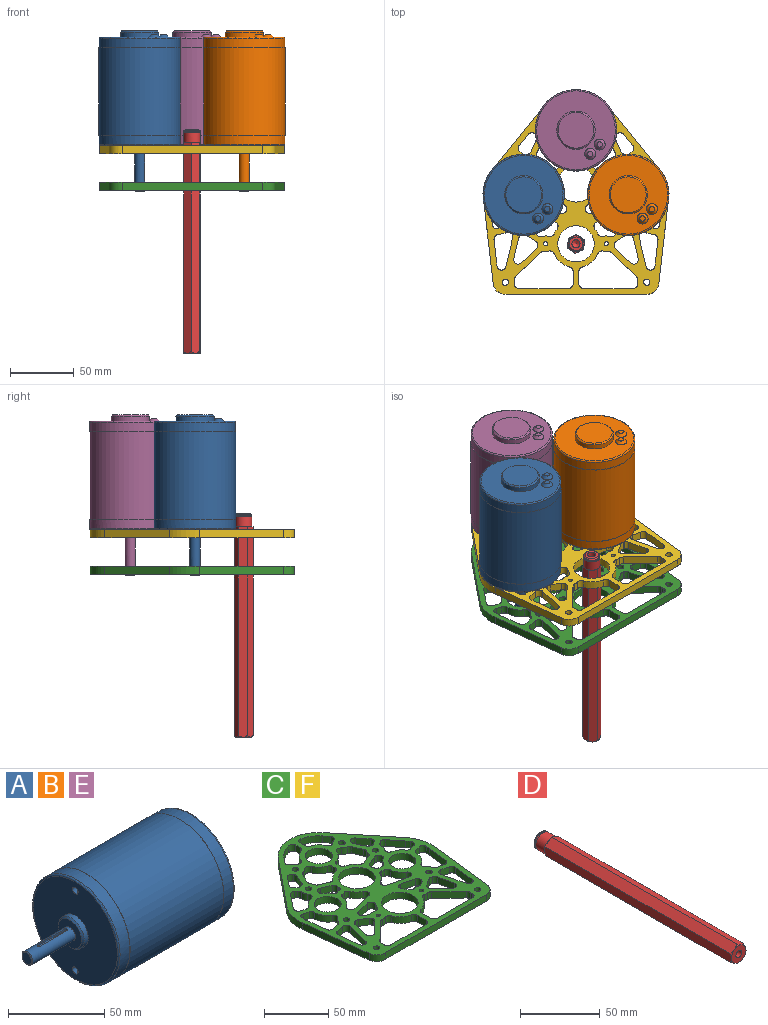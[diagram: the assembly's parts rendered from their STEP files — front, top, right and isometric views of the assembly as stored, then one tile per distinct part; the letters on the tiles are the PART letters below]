
ASSEMBLY  parts=6 mates=5
PART A: 33 faces, bbox 125.8x69x69 mm
  f0: cone r=4mm half-angle=45deg, axis (1,0,0), area 16.7mm2, adj f18,f22
  f1: cone r=9.53mm half-angle=45deg, axis (1,0,0), area 81.4mm2, adj f13,f27
  f2: cone r=14.02mm half-angle=45deg, axis (-1,0,0), area 131.2mm2, adj f17,f23
  f3: cone r=2.12mm half-angle=45deg, axis (-1,0,0), area 62.9mm2, adj f5,f29
  f4: cone r=2.12mm half-angle=45deg, axis (-1,0,0), area 62.9mm2, adj f6,f28
  f5: cylinder r=4.32mm len=8.64mm, axis (-1,0,0), area 1.3mm2, adj f3,f21
  f6: cylinder r=4.32mm len=8.64mm, axis (-1,0,0), area 1.3mm2, adj f4,f21
  f7: cone r=2.02mm half-angle=59deg, axis (-1,0,0), area 14.9mm2, adj f8
  f8: cylinder r=2.02mm len=13.61mm, axis (-1,0,0), area 172.7mm2, adj f7,f26
  f9: cone r=2.02mm half-angle=59deg, axis (-1,0,0), area 14.9mm2, adj f10
  f10: cylinder r=2.02mm len=13.61mm, axis (-1,0,0), area 172.7mm2, adj f9,f26
  f11: torus R=30.88mm, axis (1,0,0), area 311mm2, adj f16,f21
  f12: torus R=30.88mm, axis (-1,0,0), area 311mm2, adj f14,f26
  f13: cylinder r=9.53mm len=19.05mm, axis (1,0,0), area 178.6mm2, adj f1,f26
  f14: cylinder r=31.88mm len=63.75mm, axis (1,0,0), area 1448mm2, adj f12,f25
  f15: cylinder r=32mm len=68.76mm, axis (1,0,0), area 13826.1mm2, adj f24,f25
  f16: cylinder r=31.88mm len=63.75mm, axis (1,0,0), area 1448mm2, adj f11,f24
  f17: cylinder r=15.04mm len=30.07mm, axis (1,0,0), area 376.4mm2, adj f2,f21
  f18: cylinder r=4mm len=31.1mm, axis (1,0,0), area 739mm2, adj f0,f19,f20,f27,f31,f32
  f19: cylinder r=1mm len=2mm, axis (0,0,1), area 3.4mm2, adj f18,f30,f31,f32
  f20: cylinder r=1mm len=2mm, axis (0,0,-1), area 3.4mm2, adj f18,f30,f31,f32
  f21: plane 61.75x61.75mm, normal (1,0,0), area 2167.7mm2, adj f5,f6,f11,f17
  f22: plane 7x7mm, normal (-1,0,0), area 38.5mm2, adj f0
  f23: plane 28.04x28.04mm, normal (1,0,0), area 617.6mm2, adj f2
  f24: plane 64.01x64.01mm, normal (1,0,0), area 25.5mm2, adj f15,f16
  f25: plane 64.01x64.01mm, normal (-1,0,0), area 25.5mm2, adj f14,f15
  f26: plane 61.75x61.75mm, normal (-1,0,0), area 2684.5mm2, adj f8,f10,f12,f13
  f27: plane 17.02x17.02mm, normal (-1,0,0), area 177.2mm2, adj f1,f18
  f28: plane 4.24x4.24mm, normal (1,0,0), area 14.1mm2, adj f4
  f29: plane 4.24x4.24mm, normal (1,0,0), area 14.1mm2, adj f3
  f30: plane 21.5x2mm, normal (0,0,1), area 42.1mm2, adj f19,f20,f31,f32
  f31: plane 19.5x1.07mm, normal (0,-1,0), area 20.9mm2, adj f18,f19,f20,f30
  f32: plane 19.5x1.07mm, normal (0,1,0), area 20.9mm2, adj f18,f19,f20,f30
PART B: same geometry as A
PART C: 245 faces, bbox 145.6x160.4x6.4 mm
  f0: plane 160.41x145.59mm, normal (0,0,1), area 8119.2mm2, adj f2,f3,f4,f5,f6,f7,f8,f9
  f1: plane 160.41x145.59mm, normal (0,0,-1), area 8119.2mm2, adj f2,f3,f4,f5,f6,f7,f8,f9
  f2: plane 50.67x41.07mm, normal (-0.78,0.63,0), area 414.1mm2, adj f0,f1,f3,f26
  f3: cylinder r=31.75mm len=23.61mm, axis (0,0,-1), area 160.3mm2, adj f0,f1,f2,f4
  f4: plane 65.95x7.56mm, normal (-0.99,-0.11,0), area 421.5mm2, adj f0,f1,f3,f5
  f5: cylinder r=9.53mm len=10.07mm, axis (0,0,-1), area 92mm2, adj f0,f1,f4,f6
  f6: plane 110.52x6.35mm, normal (0,-1,0), area 701.8mm2, adj f0,f1,f5,f7
  f7: cylinder r=9.53mm len=9.46mm, axis (0,0,-1), area 88.1mm2, adj f0,f1,f6,f8
  f8: plane 65.95x7.56mm, normal (0.99,-0.11,0), area 421.5mm2, adj f0,f1,f7,f9
  f9: cylinder r=31.75mm len=23.61mm, axis (0,0,-1), area 160.3mm2, adj f0,f1,f8,f10
  f10: plane 50.67x41.07mm, normal (0.78,0.63,0), area 414.1mm2, adj f0,f1,f9,f26
  f11: cylinder r=14.27mm len=28.55mm, axis (0,0,-1), area 569.5mm2, adj f0,f1
  f12: cylinder r=14.27mm len=28.55mm, axis (0,0,-1), area 569.5mm2, adj f0,f1
  f13: cylinder r=10.52mm len=21.03mm, axis (0,0,-1), area 419.6mm2, adj f0,f1
  f14: cylinder r=10.52mm len=21.03mm, axis (0,0,-1), area 419.6mm2, adj f0,f1
  f15: cylinder r=2.49mm len=6.35mm, axis (0,0,-1), area 99.3mm2, adj f0,f1
  f16: cylinder r=2.49mm len=6.35mm, axis (0,0,-1), area 99.3mm2, adj f0,f1
  f17: cylinder r=1.59mm len=6.35mm, axis (0,0,-1), area 63.3mm2, adj f0,f1
  f18: cylinder r=1.59mm len=6.35mm, axis (0,0,-1), area 63.3mm2, adj f0,f1
  f19: cylinder r=2.49mm len=6.35mm, axis (0,0,-1), area 99.3mm2, adj f0,f1
  f20: cylinder r=2.49mm len=6.35mm, axis (0,0,-1), area 99.3mm2, adj f0,f1
  f21: cylinder r=2.49mm len=6.35mm, axis (0,0,-1), area 99.3mm2, adj f0,f1
  f22: cylinder r=2.49mm len=6.35mm, axis (0,0,-1), area 99.3mm2, adj f0,f1
  f23: cylinder r=2.49mm len=6.35mm, axis (0,0,-1), area 99.3mm2, adj f0,f1
  f24: cylinder r=2.49mm len=6.35mm, axis (0,0,-1), area 99.3mm2, adj f0,f1
  f25: cylinder r=10.52mm len=21.03mm, axis (0,0,-1), area 419.6mm2, adj f0,f1
  f26: cylinder r=31.72mm len=49.28mm, axis (0,0,-1), area 358.4mm2, adj f0,f1,f2,f10
  f27: plane 20.67x6.35mm, normal (0.99,0.11,0), area 132.1mm2, adj f0,f1,f30,f31
  f28: plane 22.48x6.35mm, normal (-0.97,0.23,0), area 146.7mm2, adj f0,f1,f30,f32
  f29: plane 7.68x6.35mm, normal (0.23,-0.97,0), area 50.1mm2, adj f0,f1,f31,f32
  f30: cylinder r=3.56mm len=6.99mm, axis (0,0,-1), area 63.1mm2, adj f0,f1,f27,f28
  f31: cylinder r=3.56mm len=6.35mm, axis (0,0,1), area 32.8mm2, adj f0,f1,f27,f29
  f32: cylinder r=3.56mm len=6.35mm, axis (0,0,1), area 45.9mm2, adj f0,f1,f28,f29
  f33: plane 6.35x5.15mm, normal (-1,0,0), area 32.7mm2, adj f0,f1,f38,f39
  f34: cylinder r=7.06mm len=6.35mm, axis (0,0,1), area 24.9mm2, adj f0,f1,f40,f41
  f35: plane 6.35x4.74mm, normal (0.78,-0.63,0), area 38.8mm2, adj f0,f1,f37,f41
  f36: cylinder r=15.09mm len=9.29mm, axis (0,0,1), area 83.7mm2, adj f0,f1,f38,f40
  f37: cylinder r=27.15mm len=14.37mm, axis (0,0,1), area 110.2mm2, adj f0,f1,f35,f39
  f38: cylinder r=3.56mm len=6.35mm, axis (0,0,1), area 28.3mm2, adj f0,f1,f33,f36
  f39: cylinder r=3.56mm len=6.35mm, axis (0,0,1), area 41.1mm2, adj f0,f1,f33,f37
  f40: cylinder r=3.56mm len=6.35mm, axis (0,0,1), area 46.4mm2, adj f0,f1,f34,f36
  f41: cylinder r=3.56mm len=6.35mm, axis (0,0,1), area 43.9mm2, adj f0,f1,f34,f35
  f42: cylinder r=15.09mm len=12.35mm, axis (0,0,1), area 94.7mm2, adj f0,f1,f48,f52
  f43: cylinder r=27.18mm len=6.35mm, axis (0,0,1), area 25.5mm2, adj f0,f1,f45,f49
  f44: cylinder r=7.06mm len=6.35mm, axis (0,0,1), area 30.6mm2, adj f0,f1,f50,f52
  f45: plane 20.33x6.35mm, normal (-0.99,0.11,0), area 129.9mm2, adj f0,f1,f43,f51
  f46: plane 6.9x6.35mm, normal (0.23,0.97,0), area 45mm2, adj f0,f1,f50,f51
  f47: plane 6.35x4.98mm, normal (0.28,-0.96,0), area 32.9mm2, adj f0,f1,f48,f49
  f48: cylinder r=3.56mm len=6.35mm, axis (0,0,1), area 28.3mm2, adj f0,f1,f42,f47
  f49: cylinder r=3.56mm len=6.35mm, axis (0,0,1), area 41.1mm2, adj f0,f1,f43,f47
  f50: cylinder r=3.56mm len=6.35mm, axis (0,0,1), area 22.3mm2, adj f0,f1,f44,f46
  f51: cylinder r=3.56mm len=6.35mm, axis (0,0,1), area 38.1mm2, adj f0,f1,f45,f46
  f52: cylinder r=3.56mm len=6.35mm, axis (0,0,1), area 46.4mm2, adj f0,f1,f42,f44
  f53: plane 6.35x4.98mm, normal (-0.28,-0.96,0), area 32.9mm2, adj f0,f1,f61,f62
  f54: cylinder r=27.18mm len=6.35mm, axis (0,0,1), area 25.5mm2, adj f0,f1,f55,f61
  f55: plane 20.33x6.35mm, normal (0.99,0.11,0), area 129.9mm2, adj f0,f1,f54,f60
  f56: cylinder r=15.09mm len=12.35mm, axis (0,0,1), area 94.7mm2, adj f0,f1,f62,f63
  f57: cylinder r=7.06mm len=6.35mm, axis (0,0,1), area 30.6mm2, adj f0,f1,f59,f63
  f58: plane 6.9x6.35mm, normal (-0.23,0.97,0), area 45mm2, adj f0,f1,f59,f60
  f59: cylinder r=3.56mm len=6.35mm, axis (0,0,1), area 22.3mm2, adj f0,f1,f57,f58
  f60: cylinder r=3.56mm len=6.35mm, axis (0,0,-1), area 38.1mm2, adj f0,f1,f55,f58
  f61: cylinder r=3.56mm len=6.35mm, axis (0,0,1), area 41.1mm2, adj f0,f1,f53,f54
  f62: cylinder r=3.56mm len=6.35mm, axis (0,0,1), area 28.3mm2, adj f0,f1,f53,f56
  f63: cylinder r=3.56mm len=6.35mm, axis (0,0,1), area 46.4mm2, adj f0,f1,f56,f57
  f64: plane 6.35x2.63mm, normal (1,0,0), area 16.7mm2, adj f0,f1,f75,f76
  f65: cylinder r=18.85mm len=9.72mm, axis (0,0,1), area 74.9mm2, adj f0,f1,f74,f75
  f66: cylinder r=7.06mm len=6.35mm, axis (0,0,1), area 18.2mm2, adj f0,f1,f72,f73
  f67: cylinder r=15.09mm len=9.29mm, axis (0,0,1), area 83.7mm2, adj f0,f1,f76,f77
  f68: cylinder r=7.06mm len=6.35mm, axis (0,0,1), area 31.4mm2, adj f0,f1,f71,f77
  f69: plane 8.91x6.35mm, normal (-0.41,0.91,0), area 61.9mm2, adj f0,f1,f73,f74
  f70: plane 9.44x6.35mm, normal (-0.91,-0.41,0), area 65.6mm2, adj f0,f1,f71,f72
  f71: cylinder r=3.56mm len=6.35mm, axis (0,0,1), area 22.3mm2, adj f0,f1,f68,f70
  f72: cylinder r=3.56mm len=6.35mm, axis (0,0,1), area 22.3mm2, adj f0,f1,f66,f70
  f73: cylinder r=3.56mm len=6.35mm, axis (0,0,1), area 22.3mm2, adj f0,f1,f66,f69
  f74: cylinder r=3.56mm len=6.35mm, axis (0,0,1), area 29.5mm2, adj f0,f1,f65,f69
  f75: cylinder r=3.56mm len=6.35mm, axis (0,0,1), area 29.5mm2, adj f0,f1,f64,f65
  f76: cylinder r=3.56mm len=6.35mm, axis (0,0,1), area 28.3mm2, adj f0,f1,f64,f67
  f77: cylinder r=3.56mm len=6.35mm, axis (0,0,1), area 46.4mm2, adj f0,f1,f67,f68
  f78: cylinder r=15.09mm len=9.29mm, axis (0,0,1), area 83.7mm2, adj f0,f1,f83,f86
  f79: cylinder r=27.15mm len=14.37mm, axis (0,0,1), area 110.2mm2, adj f0,f1,f81,f84
  f80: cylinder r=7.06mm len=6.35mm, axis (0,0,1), area 24.9mm2, adj f0,f1,f85,f86
  f81: plane 6.35x4.74mm, normal (-0.78,-0.63,0), area 38.8mm2, adj f0,f1,f79,f85
  f82: plane 6.35x5.15mm, normal (1,0,0), area 32.7mm2, adj f0,f1,f83,f84
  f83: cylinder r=3.56mm len=6.35mm, axis (0,0,1), area 28.3mm2, adj f0,f1,f78,f82
  f84: cylinder r=3.56mm len=6.35mm, axis (0,0,1), area 41.1mm2, adj f0,f1,f79,f82
  f85: cylinder r=3.56mm len=6.35mm, axis (0,0,1), area 43.9mm2, adj f0,f1,f80,f81
  f86: cylinder r=3.56mm len=6.35mm, axis (0,0,1), area 46.4mm2, adj f0,f1,f78,f80
  f87: cylinder r=18.85mm len=6.35mm, axis (0,0,1), area 29.3mm2, adj f0,f1,f92,f93
  f88: cylinder r=6.16mm len=6.35mm, axis (0,0,1), area 28.3mm2, adj f0,f1,f91,f93
  f89: plane 6.35x2.89mm, normal (-0.53,0.85,0), area 21.5mm2, adj f0,f1,f91,f94
  f90: plane 12.59x6.35mm, normal (-0.23,-0.97,0), area 82.1mm2, adj f0,f1,f92,f94
  f91: cylinder r=3.56mm len=6.35mm, axis (0,0,1), area 20.9mm2, adj f0,f1,f88,f89
  f92: cylinder r=3.56mm len=6.35mm, axis (0,0,1), area 55.7mm2, adj f0,f1,f87,f90
  f93: cylinder r=3.56mm len=6.35mm, axis (0,0,1), area 34mm2, adj f0,f1,f87,f88
  f94: cylinder r=3.56mm len=6.49mm, axis (0,0,1), area 53.2mm2, adj f0,f1,f89,f90
  f95: cylinder r=18.85mm len=7.91mm, axis (0,0,1), area 71mm2, adj f0,f1,f101,f102
  f96: cylinder r=15.09mm len=11.01mm, axis (0,0,1), area 84.8mm2, adj f0,f1,f99,f100
  f97: plane 6.35x2.57mm, normal (0.21,-0.98,0), area 16.7mm2, adj f0,f1,f100,f102
  f98: plane 20.07x6.35mm, normal (-0.23,0.97,0), area 130.9mm2, adj f0,f1,f99,f101
  f99: cylinder r=3.56mm len=6.54mm, axis (0,0,1), area 63.2mm2, adj f0,f1,f96,f98
  f100: cylinder r=3.56mm len=6.35mm, axis (0,0,1), area 28.3mm2, adj f0,f1,f96,f97
  f101: cylinder r=3.56mm len=6.58mm, axis (0,0,1), area 54.3mm2, adj f0,f1,f95,f98
  f102: cylinder r=3.56mm len=6.35mm, axis (0,0,1), area 29.5mm2, adj f0,f1,f95,f97
  f103: cylinder r=15.09mm len=11.01mm, axis (0,0,1), area 84.8mm2, adj f0,f1,f109,f110
  f104: cylinder r=18.85mm len=7.91mm, axis (0,0,1), area 71mm2, adj f0,f1,f107,f108
  f105: plane 20.07x6.35mm, normal (0.23,0.97,0), area 130.9mm2, adj f0,f1,f108,f110
  f106: plane 6.35x2.57mm, normal (-0.21,-0.98,0), area 16.7mm2, adj f0,f1,f107,f109
  f107: cylinder r=3.56mm len=6.35mm, axis (0,0,1), area 29.5mm2, adj f0,f1,f104,f106
  f108: cylinder r=3.56mm len=6.58mm, axis (0,0,1), area 54.3mm2, adj f0,f1,f104,f105
  f109: cylinder r=3.56mm len=6.35mm, axis (0,0,1), area 28.3mm2, adj f0,f1,f103,f106
  f110: cylinder r=3.56mm len=6.54mm, axis (0,0,1), area 63.2mm2, adj f0,f1,f103,f105
  f111: cylinder r=18.85mm len=6.35mm, axis (0,0,1), area 11.9mm2, adj f0,f1,f118,f119
  f112: cylinder r=15.09mm len=6.35mm, axis (0,0,1), area 47.5mm2, adj f0,f1,f116,f120
  f113: cylinder r=7.06mm len=6.35mm, axis (0,0,1), area 1.5mm2, adj f0,f1,f117,f120
  f114: plane 8.91x6.35mm, normal (-0.41,-0.91,0), area 61.9mm2, adj f0,f1,f117,f119
  f115: plane 6.35x2.57mm, normal (-0.21,0.98,0), area 16.7mm2, adj f0,f1,f116,f118
  f116: cylinder r=3.56mm len=6.35mm, axis (0,0,1), area 28.3mm2, adj f0,f1,f112,f115
  f117: cylinder r=3.56mm len=6.35mm, axis (0,0,1), area 22.3mm2, adj f0,f1,f113,f114
  f118: cylinder r=3.56mm len=6.35mm, axis (0,0,1), area 29.5mm2, adj f0,f1,f111,f115
  f119: cylinder r=3.56mm len=6.35mm, axis (0,0,1), area 29.5mm2, adj f0,f1,f111,f114
  f120: cylinder r=3.56mm len=6.35mm, axis (0,0,1), area 46.4mm2, adj f0,f1,f112,f113
  f121: plane 7.35x6.35mm, normal (-0.53,-0.85,0), area 54.8mm2, adj f0,f1,f127,f129
  f122: cylinder r=6.16mm len=6.35mm, axis (0,0,1), area 0.9mm2, adj f0,f1,f128,f129
  f123: cylinder r=7.06mm len=6.35mm, axis (0,0,1), area 3.8mm2, adj f0,f1,f126,f127
  f124: plane 15.73x6.35mm, normal (0.97,-0.23,0), area 102.6mm2, adj f0,f1,f126,f130
  f125: plane 11.91x11.31mm, normal (-0.69,0.72,0), area 104.3mm2, adj f0,f1,f128,f130
  f126: cylinder r=3.56mm len=6.35mm, axis (0,0,1), area 22.3mm2, adj f0,f1,f123,f124
  f127: cylinder r=3.56mm len=6.35mm, axis (0,0,1), area 22.3mm2, adj f0,f1,f121,f123
  f128: cylinder r=3.56mm len=6.35mm, axis (0,0,1), area 20.9mm2, adj f0,f1,f122,f125
  f129: cylinder r=3.56mm len=6.35mm, axis (0,0,1), area 20.9mm2, adj f0,f1,f121,f122
  f130: cylinder r=3.56mm len=6.35mm, axis (0,0,1), area 57.9mm2, adj f0,f1,f124,f125
  f131: cylinder r=18.85mm len=6.35mm, axis (0,0,1), area 29.3mm2, adj f0,f1,f136,f137
  f132: cylinder r=6.16mm len=6.35mm, axis (0,0,1), area 28.3mm2, adj f0,f1,f135,f137
  f133: plane 12.59x6.35mm, normal (0.23,-0.97,0), area 82.1mm2, adj f0,f1,f136,f138
  f134: plane 6.35x2.89mm, normal (0.53,0.85,0), area 21.5mm2, adj f0,f1,f135,f138
  f135: cylinder r=3.56mm len=6.35mm, axis (0,0,1), area 20.9mm2, adj f0,f1,f132,f134
  f136: cylinder r=3.56mm len=6.35mm, axis (0,0,1), area 55.7mm2, adj f0,f1,f131,f133
  f137: cylinder r=3.56mm len=6.35mm, axis (0,0,-1), area 34mm2, adj f0,f1,f131,f132
  f138: cylinder r=3.56mm len=6.49mm, axis (0,0,1), area 53.2mm2, adj f0,f1,f133,f134
  f139: plane 7.35x6.35mm, normal (0.53,-0.85,0), area 54.8mm2, adj f0,f1,f145,f147
  f140: cylinder r=6.16mm len=6.35mm, axis (0,0,1), area 0.9mm2, adj f0,f1,f146,f147
  f141: cylinder r=7.06mm len=6.35mm, axis (0,0,1), area 3.8mm2, adj f0,f1,f144,f145
  f142: plane 11.91x11.31mm, normal (0.69,0.72,0), area 104.3mm2, adj f0,f1,f146,f148
  f143: plane 15.73x6.35mm, normal (-0.97,-0.23,0), area 102.6mm2, adj f0,f1,f144,f148
  f144: cylinder r=3.56mm len=6.35mm, axis (0,0,1), area 22.3mm2, adj f0,f1,f141,f143
  f145: cylinder r=3.56mm len=6.35mm, axis (0,0,1), area 22.3mm2, adj f0,f1,f139,f141
  f146: cylinder r=3.56mm len=6.35mm, axis (0,0,1), area 20.9mm2, adj f0,f1,f140,f142
  f147: cylinder r=3.56mm len=6.35mm, axis (0,0,1), area 20.9mm2, adj f0,f1,f139,f140
  f148: cylinder r=3.56mm len=6.35mm, axis (0,0,1), area 57.9mm2, adj f0,f1,f142,f143
  f149: plane 7.68x6.35mm, normal (-0.23,-0.97,0), area 50.1mm2, adj f0,f1,f152,f154
  f150: plane 22.48x6.35mm, normal (0.97,0.23,0), area 146.7mm2, adj f0,f1,f153,f154
  f151: plane 20.67x6.35mm, normal (-0.99,0.11,0), area 132.1mm2, adj f0,f1,f152,f153
  f152: cylinder r=3.56mm len=6.35mm, axis (0,0,-1), area 32.8mm2, adj f0,f1,f149,f151
  f153: cylinder r=3.56mm len=6.99mm, axis (0,0,1), area 63.1mm2, adj f0,f1,f150,f151
  f154: cylinder r=3.56mm len=6.35mm, axis (0,0,1), area 45.9mm2, adj f0,f1,f149,f150
  f155: plane 9.44x6.35mm, normal (0.91,-0.41,0), area 65.6mm2, adj f0,f1,f166,f167
  f156: cylinder r=7.06mm len=6.35mm, axis (0,0,1), area 18.2mm2, adj f0,f1,f162,f166
  f157: cylinder r=18.85mm len=9.72mm, axis (0,0,1), area 74.9mm2, adj f0,f1,f163,f164
  f158: cylinder r=7.06mm len=6.35mm, axis (0,0,1), area 31.4mm2, adj f0,f1,f167,f168
  f159: cylinder r=15.09mm len=9.29mm, axis (0,0,1), area 83.7mm2, adj f0,f1,f165,f168
  f160: plane 6.35x2.63mm, normal (-1,0,0), area 16.7mm2, adj f0,f1,f164,f165
  f161: plane 8.91x6.35mm, normal (0.41,0.91,0), area 61.9mm2, adj f0,f1,f162,f163
  f162: cylinder r=3.56mm len=6.35mm, axis (0,0,1), area 22.3mm2, adj f0,f1,f156,f161
  f163: cylinder r=3.56mm len=6.35mm, axis (0,0,1), area 29.5mm2, adj f0,f1,f157,f161
  f164: cylinder r=3.56mm len=6.35mm, axis (0,0,1), area 29.5mm2, adj f0,f1,f157,f160
  f165: cylinder r=3.56mm len=6.35mm, axis (0,0,1), area 28.3mm2, adj f0,f1,f159,f160
  f166: cylinder r=3.56mm len=6.35mm, axis (0,0,1), area 22.3mm2, adj f0,f1,f155,f156
  f167: cylinder r=3.56mm len=6.35mm, axis (0,0,1), area 22.3mm2, adj f0,f1,f155,f158
  f168: cylinder r=3.56mm len=6.35mm, axis (0,0,1), area 46.4mm2, adj f0,f1,f158,f159
  f169: plane 12.66x10.26mm, normal (0.78,-0.63,0), area 103.5mm2, adj f0,f1,f170,f176
  f170: cylinder r=27.18mm len=6.35mm, axis (0,0,1), area 25.5mm2, adj f0,f1,f169,f177
  f171: cylinder r=15.09mm len=9.29mm, axis (0,0,1), area 72.7mm2, adj f0,f1,f178,f179
  f172: cylinder r=7.06mm len=6.35mm, axis (0,0,1), area 35.6mm2, adj f0,f1,f175,f179
  f173: plane 6.35x4.98mm, normal (0.28,0.96,0), area 32.9mm2, adj f0,f1,f177,f178
  f174: plane 6.35x1.79mm, normal (-0.63,-0.78,0), area 14.6mm2, adj f0,f1,f175,f176
  f175: cylinder r=3.56mm len=6.35mm, axis (0,0,1), area 22.3mm2, adj f0,f1,f172,f174
  f176: cylinder r=3.56mm len=6.35mm, axis (0,0,1), area 35.5mm2, adj f0,f1,f169,f174
  f177: cylinder r=3.56mm len=6.35mm, axis (0,0,1), area 41.1mm2, adj f0,f1,f170,f173
  f178: cylinder r=3.56mm len=6.35mm, axis (0,0,1), area 28.3mm2, adj f0,f1,f171,f173
  f179: cylinder r=3.56mm len=6.35mm, axis (0,0,1), area 46.4mm2, adj f0,f1,f171,f172
  f180: plane 6.35x4.98mm, normal (-0.28,0.96,0), area 32.9mm2, adj f0,f1,f188,f189
  f181: cylinder r=27.18mm len=6.35mm, axis (0,0,1), area 25.5mm2, adj f0,f1,f182,f189
  f182: plane 12.66x10.26mm, normal (-0.78,-0.63,0), area 103.5mm2, adj f0,f1,f181,f187
  f183: cylinder r=7.06mm len=6.35mm, axis (0,0,1), area 35.6mm2, adj f0,f1,f186,f190
  f184: cylinder r=15.09mm len=9.29mm, axis (0,0,1), area 72.7mm2, adj f0,f1,f188,f190
  f185: plane 6.35x1.79mm, normal (0.63,-0.78,0), area 14.6mm2, adj f0,f1,f186,f187
  f186: cylinder r=3.56mm len=6.35mm, axis (0,0,1), area 22.3mm2, adj f0,f1,f183,f185
  f187: cylinder r=3.56mm len=6.35mm, axis (0,0,-1), area 35.5mm2, adj f0,f1,f182,f185
  f188: cylinder r=3.56mm len=6.35mm, axis (0,0,1), area 28.3mm2, adj f0,f1,f180,f184
  f189: cylinder r=3.56mm len=6.35mm, axis (0,0,1), area 41.1mm2, adj f0,f1,f180,f181
  f190: cylinder r=3.56mm len=6.35mm, axis (0,0,1), area 46.4mm2, adj f0,f1,f183,f184
  f191: plane 9.92x6.35mm, normal (1,0,0), area 63mm2, adj f0,f1,f199,f200
  f192: plane 39.2x6.35mm, normal (0,1,0), area 248.9mm2, adj f0,f1,f199,f202
  f193: cylinder r=7.06mm len=6.35mm, axis (0,0,1), area 13.9mm2, adj f0,f1,f198,f202
  f194: cylinder r=18.85mm len=12.3mm, axis (0,0,1), area 106.2mm2, adj f0,f1,f200,f201
  f195: cylinder r=6.16mm len=6.35mm, axis (0,0,1), area 20.3mm2, adj f0,f1,f197,f201
  f196: plane 19.69x18.71mm, normal (-0.69,-0.72,0), area 172.5mm2, adj f0,f1,f197,f198
  f197: cylinder r=3.56mm len=6.35mm, axis (0,0,1), area 20.9mm2, adj f0,f1,f195,f196
  f198: cylinder r=3.56mm len=6.35mm, axis (0,0,1), area 22.3mm2, adj f0,f1,f193,f196
  f199: cylinder r=3.56mm len=6.35mm, axis (0,0,1), area 35.5mm2, adj f0,f1,f191,f192
  f200: cylinder r=3.56mm len=6.35mm, axis (0,0,1), area 29.5mm2, adj f0,f1,f191,f194
  f201: cylinder r=3.56mm len=6.35mm, axis (0,0,1), area 34mm2, adj f0,f1,f194,f195
  f202: cylinder r=3.56mm len=6.35mm, axis (0,0,1), area 38.4mm2, adj f0,f1,f192,f193
  f203: plane 6.35x2.57mm, normal (0.21,0.98,0), area 16.7mm2, adj f0,f1,f210,f211
  f204: cylinder r=18.85mm len=6.35mm, axis (0,0,1), area 11.9mm2, adj f0,f1,f209,f210
  f205: cylinder r=15.09mm len=6.35mm, axis (0,0,1), area 47.5mm2, adj f0,f1,f211,f212
  f206: cylinder r=7.06mm len=6.35mm, axis (0,0,1), area 1.5mm2, adj f0,f1,f208,f212
  f207: plane 8.91x6.35mm, normal (0.41,-0.91,0), area 61.9mm2, adj f0,f1,f208,f209
  f208: cylinder r=3.56mm len=6.35mm, axis (0,0,1), area 22.3mm2, adj f0,f1,f206,f207
  f209: cylinder r=3.56mm len=6.35mm, axis (0,0,1), area 29.5mm2, adj f0,f1,f204,f207
  f210: cylinder r=3.56mm len=6.35mm, axis (0,0,1), area 29.5mm2, adj f0,f1,f203,f204
  f211: cylinder r=3.56mm len=6.35mm, axis (0,0,1), area 28.3mm2, adj f0,f1,f203,f205
  f212: cylinder r=3.56mm len=6.35mm, axis (0,0,1), area 46.4mm2, adj f0,f1,f205,f206
  f213: cylinder r=7.06mm len=6.35mm, axis (0,0,1), area 6.4mm2, adj f0,f1,f218,f220
  f214: cylinder r=7.06mm len=6.35mm, axis (0,0,1), area 2.4mm2, adj f0,f1,f221,f222
  f215: plane 8.82x7.15mm, normal (0.78,-0.63,0), area 72.1mm2, adj f0,f1,f219,f222
  f216: plane 9.44x6.35mm, normal (-0.91,0.41,0), area 65.6mm2, adj f0,f1,f220,f221
  f217: plane 6.35x1.79mm, normal (0.63,0.78,0), area 14.6mm2, adj f0,f1,f218,f219
  f218: cylinder r=3.56mm len=6.35mm, axis (0,0,1), area 22.3mm2, adj f0,f1,f213,f217
  f219: cylinder r=3.56mm len=6.35mm, axis (0,0,-1), area 35.5mm2, adj f0,f1,f215,f217
  f220: cylinder r=3.56mm len=6.35mm, axis (0,0,1), area 22.3mm2, adj f0,f1,f213,f216
  f221: cylinder r=3.56mm len=6.35mm, axis (0,0,1), area 22.3mm2, adj f0,f1,f214,f216
  f222: cylinder r=3.56mm len=6.35mm, axis (0,0,1), area 43.9mm2, adj f0,f1,f214,f215
  f223: plane 6.35x1.79mm, normal (-0.63,0.78,0), area 14.6mm2, adj f0,f1,f230,f231
  f224: plane 8.82x7.15mm, normal (-0.78,-0.63,0), area 72.1mm2, adj f0,f1,f231,f232
  f225: cylinder r=7.06mm len=6.35mm, axis (0,0,1), area 2.4mm2, adj f0,f1,f228,f232
  f226: cylinder r=7.06mm len=6.35mm, axis (0,0,1), area 6.4mm2, adj f0,f1,f229,f230
  f227: plane 9.44x6.35mm, normal (0.91,0.41,0), area 65.6mm2, adj f0,f1,f228,f229
  f228: cylinder r=3.56mm len=6.35mm, axis (0,0,1), area 22.3mm2, adj f0,f1,f225,f227
  f229: cylinder r=3.56mm len=6.35mm, axis (0,0,1), area 22.3mm2, adj f0,f1,f226,f227
  f230: cylinder r=3.56mm len=6.35mm, axis (0,0,1), area 22.3mm2, adj f0,f1,f223,f226
  f231: cylinder r=3.56mm len=6.35mm, axis (0,0,1), area 35.5mm2, adj f0,f1,f223,f224
  f232: cylinder r=3.56mm len=6.35mm, axis (0,0,1), area 43.9mm2, adj f0,f1,f224,f225
  f233: plane 39.19x6.35mm, normal (0,1,0), area 248.9mm2, adj f0,f1,f241,f243
  f234: cylinder r=7.06mm len=6.35mm, axis (0,0,1), area 13.8mm2, adj f0,f1,f239,f243
  f235: cylinder r=18.85mm len=12.3mm, axis (0,0,1), area 106.2mm2, adj f0,f1,f242,f244
  f236: cylinder r=6.16mm len=6.35mm, axis (0,0,1), area 20.3mm2, adj f0,f1,f240,f244
  f237: plane 9.92x6.35mm, normal (-1,0,0), area 63mm2, adj f0,f1,f241,f242
  f238: plane 19.69x18.71mm, normal (0.69,-0.72,0), area 172.5mm2, adj f0,f1,f239,f240
  f239: cylinder r=3.56mm len=6.35mm, axis (0,0,1), area 22.3mm2, adj f0,f1,f234,f238
  f240: cylinder r=3.56mm len=6.35mm, axis (0,0,1), area 20.9mm2, adj f0,f1,f236,f238
  f241: cylinder r=3.56mm len=6.35mm, axis (0,0,-1), area 35.5mm2, adj f0,f1,f233,f237
  f242: cylinder r=3.56mm len=6.35mm, axis (0,0,1), area 29.5mm2, adj f0,f1,f235,f237
  f243: cylinder r=3.56mm len=6.35mm, axis (0,0,1), area 38.4mm2, adj f0,f1,f233,f234
  f244: cylinder r=3.56mm len=6.35mm, axis (0,0,-1), area 34mm2, adj f0,f1,f235,f236
PART D: 25 faces, bbox 15.1x176.1x15.2 mm
  f0: cylinder r=2.55mm len=50.8mm, axis (0,-1,0), area 814.8mm2, adj f1,f17
  f1: cone r=2.55mm half-angle=59deg, axis (0,-1,0), area 23.9mm2, adj f0
  f2: cone r=5.34mm half-angle=45deg, axis (0,-1,0), area 51.9mm2, adj f6,f19
  f3: cone r=6.42mm half-angle=30deg, axis (0,1,0), area 4.7mm2, adj f12,f13,f17
  f4: cylinder r=3.19mm len=12.7mm, axis (0,1,0), area 254.4mm2, adj f5,f19
  f5: cone r=3.19mm half-angle=59deg, axis (0,1,0), area 37.2mm2, adj f4
  f6: cylinder r=6.34mm len=12.67mm, axis (0,-1,0), area 23.4mm2, adj f2,f18
  f7: cylinder r=5.94mm len=11.89mm, axis (0,-1,0), area 37.9mm2, adj f9,f18
  f8: cylinder r=6.34mm len=12.67mm, axis (0,-1,0), area 316.1mm2, adj f9,f10
  f9: plane 12.67x12.67mm, normal (0,1,0), area 15.2mm2, adj f7,f8
  f10: plane 14.61x13.28mm, normal (0,1,0), area 13.5mm2, adj f8,f11,f12,f13,f14,f15,f16
  f11: plane 165.61x7.81mm, normal (1,0,0.09), area 1207mm2, adj f10,f12,f16,f17,f21,f22
  f12: plane 165.61x7.15mm, normal (0.42,0,0.91), area 1207mm2, adj f3,f10,f11,f13,f17,f22
  f13: plane 165.61x6.52mm, normal (-0.57,0,0.82), area 1207mm2, adj f3,f10,f12,f14,f17,f23
  f14: plane 165.61x7.81mm, normal (-1,0,-0.09), area 1207mm2, adj f10,f13,f15,f17,f23,f24
  f15: plane 165.61x7.15mm, normal (-0.42,0,-0.91), area 1207.3mm2, adj f10,f14,f16,f17,f20,f24
  f16: plane 165.61x6.52mm, normal (0.57,0,-0.82), area 1207mm2, adj f10,f11,f15,f17,f20,f21
  f17: plane 12.83x12.81mm, normal (0,-1,0), area 108.4mm2, adj f0,f3,f11,f12,f13,f14,f15,f16
  f18: plane 12.67x12.67mm, normal (0,-1,0), area 15.2mm2, adj f6,f7
  f19: plane 10.67x10.67mm, normal (0,1,0), area 57.6mm2, adj f2,f4
  f20: cone r=6.42mm half-angle=30deg, axis (0,1,0), area 4.7mm2, adj f15,f16,f17
  f21: cone r=6.42mm half-angle=30deg, axis (0,1,0), area 4.7mm2, adj f11,f16,f17
  f22: cone r=6.42mm half-angle=30deg, axis (0,1,0), area 4.7mm2, adj f11,f12,f17
  f23: cone r=6.42mm half-angle=30deg, axis (0,1,0), area 4.7mm2, adj f13,f14,f17
  f24: cone r=6.42mm half-angle=30deg, axis (0,1,0), area 4.7mm2, adj f14,f15,f17
PART E: same geometry as A
PART F: same geometry as C
PLACE A rot(axis=(0.71,0,0.71),180deg) t=(-67.99,12.65,48.8)mm
PLACE B rot(axis=(0.71,0,0.71),180deg) t=(14.09,12.65,48.8)mm
PLACE C t=(-26.95,-25.66,13.87)mm
PLACE D rot(axis=(1,0,0),90deg) t=(-26.95,-72.7,58.89)mm
PLACE E rot(axis=(0.71,0,0.71),180deg) t=(-26.95,63.34,48.8)mm
PLACE F t=(-26.95,-25.66,42.45)mm
MATE fastened C.f7 <-> F.f7  axis (0,0,1) through (28.61,-55.82,20.22)mm
MATE revolute D.f0 <-> F.f11  axis (0,0,1) through (-26.95,-25.66,61.5)mm
MATE fastened B.f0 <-> F.f9  axis (0,0,-1) through (14.09,12.65,48.8)mm
MATE fastened A.f0 <-> F.f3  axis (0,0,-1) through (-67.99,12.65,48.8)mm
MATE fastened E.f0 <-> F.f13  axis (0,0,-1) through (-26.95,63.34,48.8)mm
